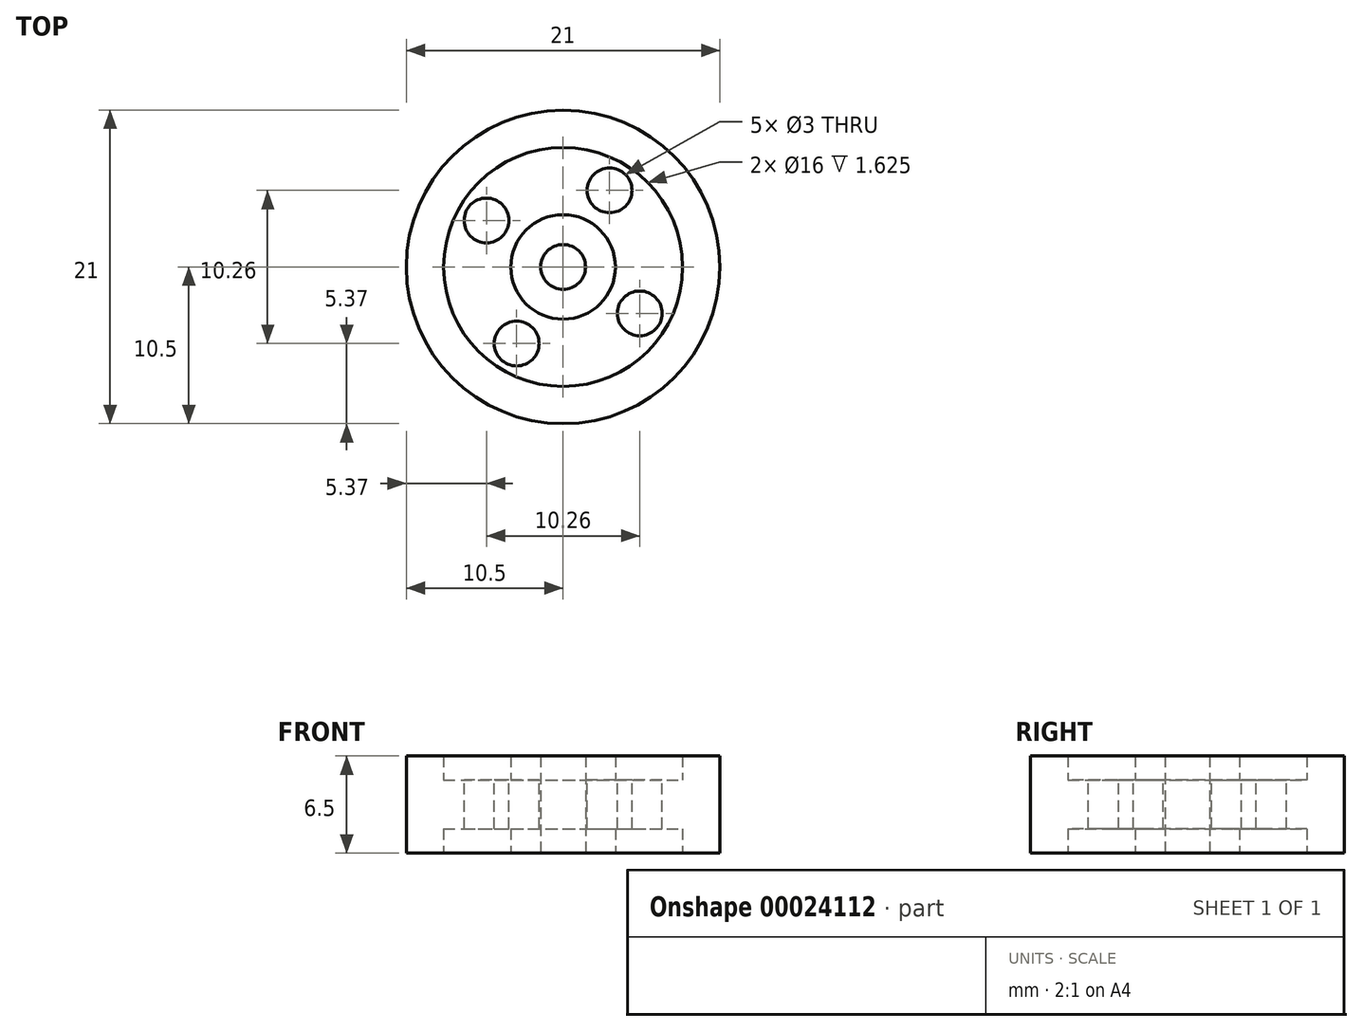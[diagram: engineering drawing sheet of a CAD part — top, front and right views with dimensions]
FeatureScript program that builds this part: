
annotation { "Feature Type Name" : "Feature", "Feature Type Description" : "" }
export const myFeature = defineFeature(function(context is Context, id is Id, definition is map)
    precondition{}
    {
        {
            var Q0;
            Q0=qCreatedBy(makeId("Front.planeOp"),FACE);
            var sketch = newSketch(context, id + "F0", { "sketchPlane" : qUnion([Q0])});
            skLineSegment(sketch, "E0", {"start": v(0, 0.04) * mm, "end": v(0, 20.57) * mm, "construction": true});
            skLineSegment(sketch, "E1", {"start": v(-1.5, 15.56) * mm, "end": v(-1.5, 9.06) * mm});
            skLineSegment(sketch, "E2", {"start": v(-1.5, 9.06) * mm, "end": v(-3.5, 9.06) * mm});
            skLineSegment(sketch, "E3", {"start": v(-3.5, 9.06) * mm, "end": v(-3.5, 10.69) * mm});
            skLineSegment(sketch, "E4", {"start": v(-3.5, 10.69) * mm, "end": v(-8, 10.69) * mm});
            skLineSegment(sketch, "E5", {"start": v(-8, 10.69) * mm, "end": v(-8, 9.06) * mm});
            skLineSegment(sketch, "E6", {"start": v(-8, 9.06) * mm, "end": v(-10.5, 9.06) * mm});
            skLineSegment(sketch, "E7", {"start": v(-10.5, 9.06) * mm, "end": v(-10.5, 15.56) * mm});
            skLineSegment(sketch, "E8", {"start": v(-10.5, 15.56) * mm, "end": v(-8, 15.56) * mm});
            skLineSegment(sketch, "E9", {"start": v(-8, 15.56) * mm, "end": v(-8, 13.94) * mm});
            skLineSegment(sketch, "E10", {"start": v(-8, 13.94) * mm, "end": v(-3.5, 13.94) * mm});
            skLineSegment(sketch, "E11", {"start": v(-3.5, 13.94) * mm, "end": v(-3.5, 15.56) * mm});
            skLineSegment(sketch, "E12", {"start": v(-3.5, 15.56) * mm, "end": v(-1.5, 15.56) * mm});
            skSolve(sketch);
        }
        {
            var Q0;
            Q0 = qSketchRegion(id + "F0", true);
            var Q1;
            Q1=sQuery(id+"F0.wireOp",EDGE,"E0");
            revolve(context, id + "F1", {"entities" : qUnion([Q0]), "axis" : qUnion([Q1]), "revolveType" : RevolveType.FULL});
        }
        {
            var Q0;
            Q0=makeQuery(id+"F1.opRevolve","SWEPT_FACE",FACE,{"disambiguationData":[OSD([sQuery(id+"F0.wireOp",EDGE,"E10")])]});
            var sketch = newSketch(context, id + "F2", { "sketchPlane" : qUnion([Q0])});
            skCircle(sketch, "E13", {"center": v(-5.13, 3.11) * mm, "radius": 1.5 * mm});
            skCircle(sketch, "E14.1.0", {"center": v(-3.11, -5.13) * mm, "radius": 1.5 * mm});
            skCircle(sketch, "E14.2.0", {"center": v(5.13, -3.11) * mm, "radius": 1.5 * mm});
            skCircle(sketch, "E14.3.0", {"center": v(3.11, 5.13) * mm, "radius": 1.5 * mm});
            skPoint(sketch, "E14.center", {"position": v(0, 0) * mm});
            skSolve(sketch);
        }
        {
            var Q0;
            Q0=makeQuery(id+"F2.imprint","IMPRINT",FACE,{"disambiguationData":[TD([[makeQuery(id+"F2.imprint","IMPRINT",EDGE,{"derivedFrom":sQuery(id+"F2.wireOp",EDGE,"E13")}),1.0]])]});
            var Q1;
            Q1=makeQuery(id+"F2.imprint","IMPRINT",FACE,{"disambiguationData":[TD([[makeQuery(id+"F2.imprint","IMPRINT",EDGE,{"derivedFrom":sQuery(id+"F2.wireOp",EDGE,"E14.3.0")}),1.0]])]});
            var Q2;
            Q2=makeQuery(id+"F2.imprint","IMPRINT",FACE,{"disambiguationData":[TD([[makeQuery(id+"F2.imprint","IMPRINT",EDGE,{"derivedFrom":sQuery(id+"F2.wireOp",EDGE,"E14.2.0")}),1.0]])]});
            var Q3;
            Q3=makeQuery(id+"F2.imprint","IMPRINT",FACE,{"disambiguationData":[TD([[makeQuery(id+"F2.imprint","IMPRINT",EDGE,{"derivedFrom":sQuery(id+"F2.wireOp",EDGE,"E14.1.0")}),1.0]])]});
            extrude(context, id + "F3", {"entities" : qUnion([Q0, Q1, Q2, Q3]), "operationType" : NewBodyOperationType.REMOVE, "oppositeDirection" : true, "depth" : 6.5 * mm});
        }
    });
